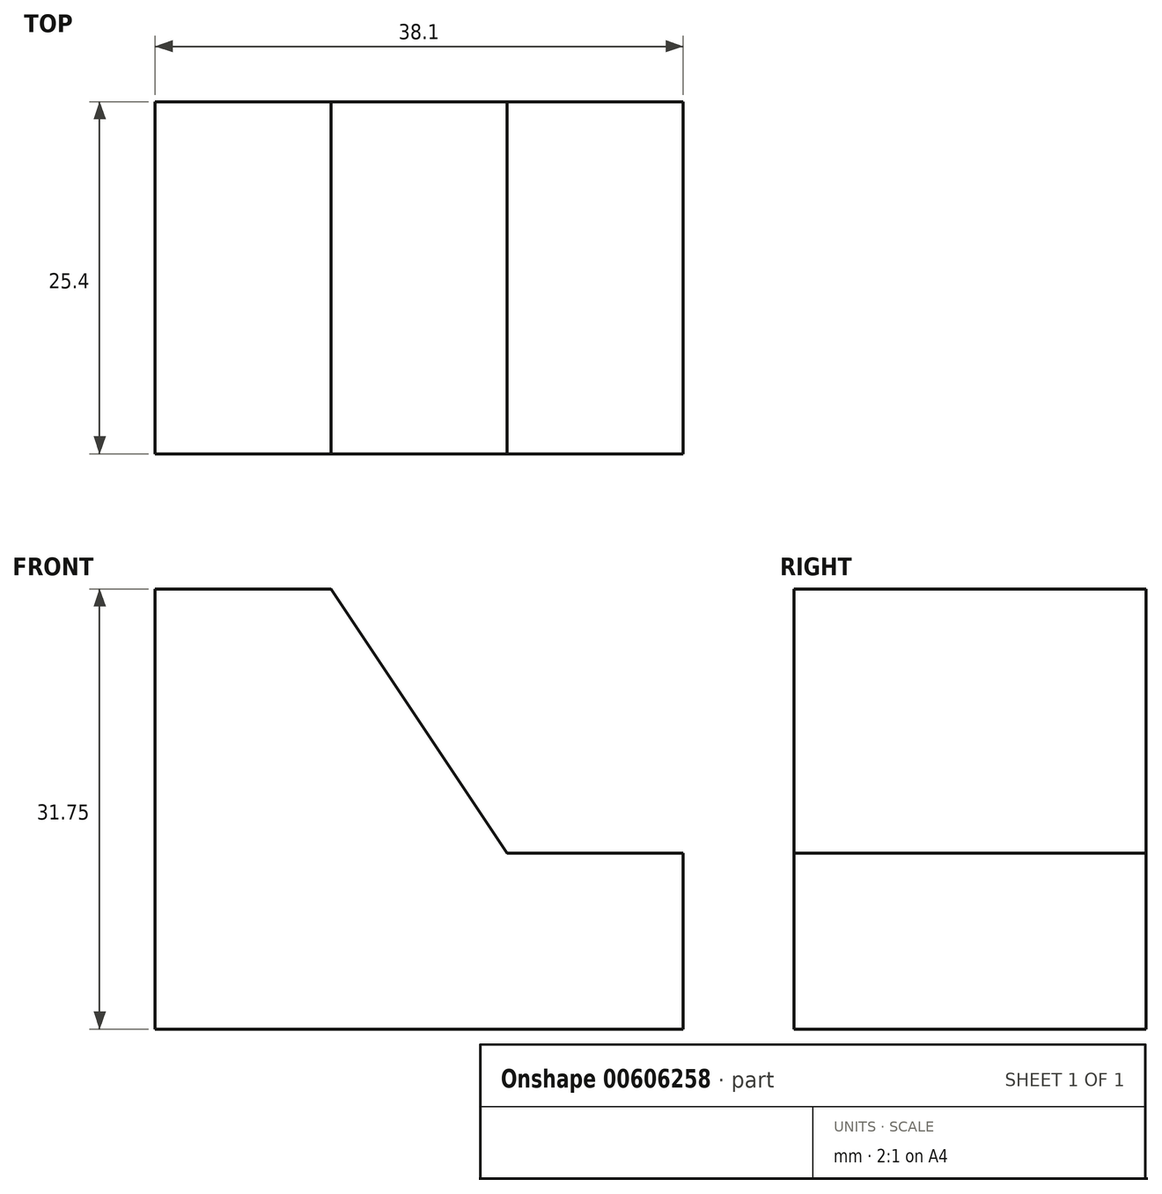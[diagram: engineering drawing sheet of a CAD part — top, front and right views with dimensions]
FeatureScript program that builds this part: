
annotation { "Feature Type Name" : "Feature", "Feature Type Description" : "" }
export const myFeature = defineFeature(function(context is Context, id is Id, definition is map)
    precondition{}
    {
        {
            var Q0;
            Q0=qCreatedBy(makeId("Front.planeOp"),FACE);
            var sketch = newSketch(context, id + "F0", { "sketchPlane" : qUnion([Q0])});
            skLineSegment(sketch, "E0", {"start": v(0, 0) * mm, "end": v(38.1, 0) * mm});
            skLineSegment(sketch, "E1", {"start": v(0, 0) * mm, "end": v(0, 31.75) * mm});
            skLineSegment(sketch, "E2", {"start": v(0, 31.75) * mm, "end": v(12.7, 31.75) * mm});
            skLineSegment(sketch, "E3", {"start": v(38.1, 0) * mm, "end": v(38.1, 12.7) * mm});
            skLineSegment(sketch, "E4", {"start": v(38.1, 12.7) * mm, "end": v(25.4, 12.7) * mm});
            skLineSegment(sketch, "E5", {"start": v(12.7, 31.75) * mm, "end": v(25.4, 12.7) * mm});
            skSolve(sketch);
        }
        {
            var Q0;
            Q0=makeQuery(id+"F0.imprint","IMPRINT",FACE,{"disambiguationData":[TD([[makeQuery(id+"F0.imprint","IMPRINT",EDGE,{"derivedFrom":sQuery(id+"F0.wireOp",EDGE,"E0")}),1.0]])]});
            extrude(context, id + "F1", {"entities" : qUnion([Q0]), "depth" : 25.4 * mm, "offsetDistance" : 25.4 * mm});
        }
    });
